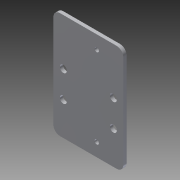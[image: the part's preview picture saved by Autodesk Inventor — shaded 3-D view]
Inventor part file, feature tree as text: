
AUTODESK INVENTOR PART (.ipt)
format: ipt  version: 2014 (Build 180170000, 170)  size: 116,224 bytes
history: native  units: in
note: dims shown in document units (in); Inventor stores cm internally (conversion verified against a paired STEP export)
features: extrude x2, fillet x1, sketch x1
ambient origin geometry x8: Origin, YZ Plane, XZ Plane, XY Plane, X Axis, Y Axis, Z Axis, Center Point
bodies: Solid1 (feature_tree)
feature tree (4):
  extrude  "Extrusion1"  Depth=2.63in
  extrude  "Extrusion4"  Depth=1.0in
  fillet  "Fillet1"  Radius=1.88in
  sketch  "Sketch4"  dims[d0=1.5in d1=2.63in d2=1.0in d3=1.88in d4=0.375in d6=0.266in d7=0.266in d8=0.266in d9=0.266in d11=0.125in d12=0.0in d14=0.25in d15=0.375in d17=1.0in d18=4.0in d31=0.163in d32=1.0in d33=0.5in d34=0.163in d35=3.0in d36=1.0in d37=1.0in d38=0.0in d39=0.25in]
